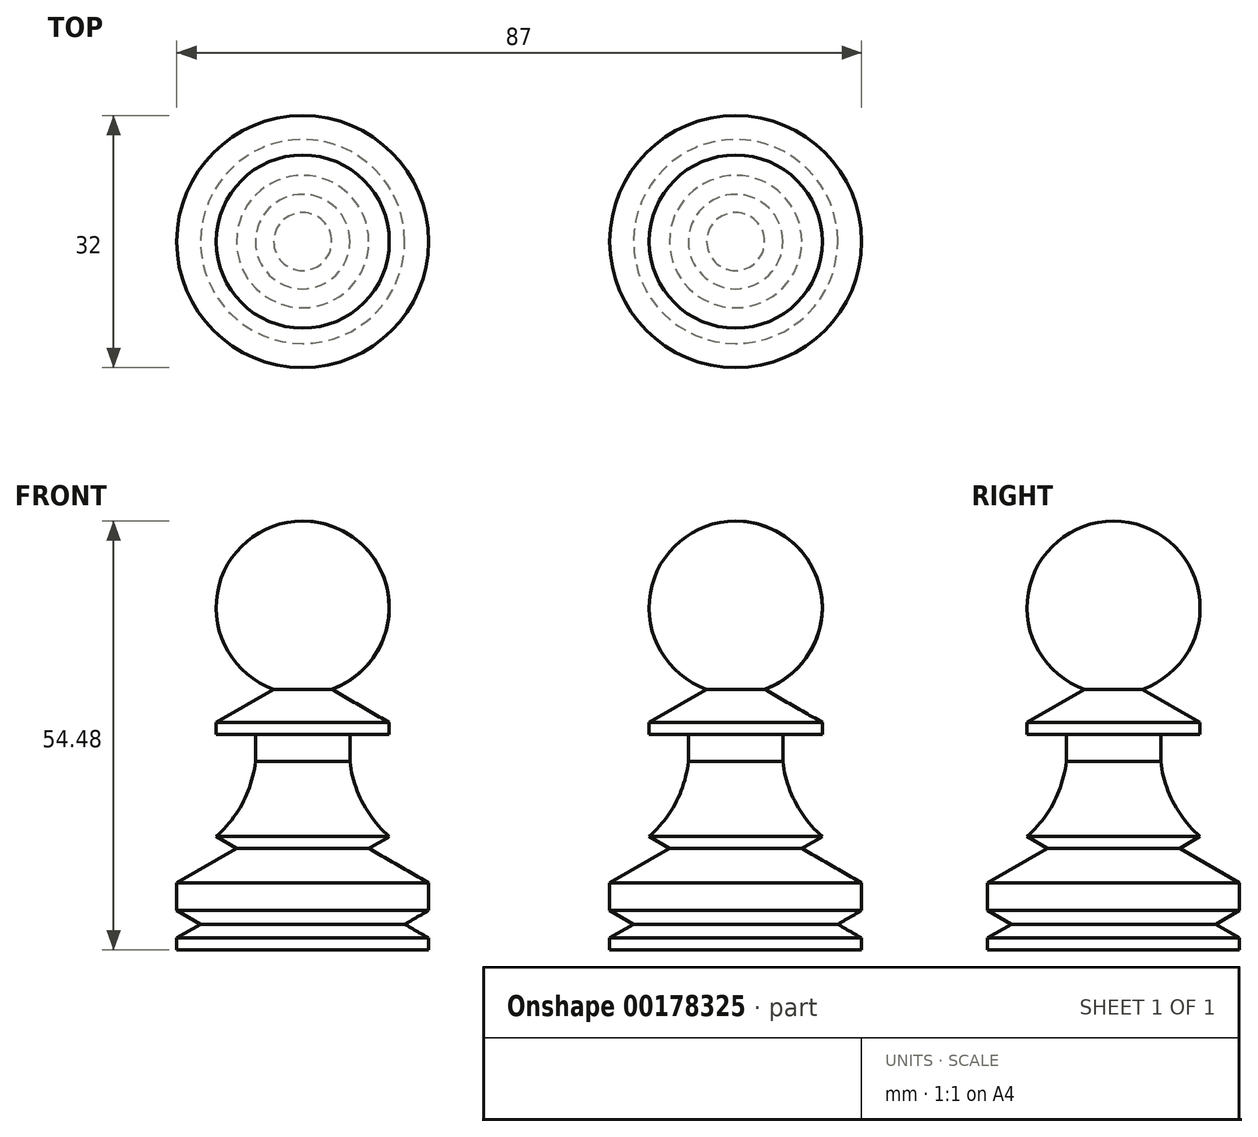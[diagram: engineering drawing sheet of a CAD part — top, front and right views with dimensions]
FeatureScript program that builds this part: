
annotation { "Feature Type Name" : "Feature", "Feature Type Description" : "" }
export const myFeature = defineFeature(function(context is Context, id is Id, definition is map)
    precondition{}
    {
        {
            var Q0;
            Q0=qCreatedBy(makeId("Front.planeOp"),FACE);
            var sketch = newSketch(context, id + "F0", { "sketchPlane" : qUnion([Q0])});
            skLineSegment(sketch, "E0", {"start": v(0, 0) * mm, "end": v(16, 0) * mm});
            skLineSegment(sketch, "E1", {"start": v(16, 0) * mm, "end": v(16, 1.5) * mm});
            skLineSegment(sketch, "E2", {"start": v(16, 1.5) * mm, "end": v(12.97, 3.25) * mm});
            skLineSegment(sketch, "E3", {"start": v(0, 0) * mm, "end": v(0, 5) * mm});
            skLineSegment(sketch, "E4", {"start": v(0, 5) * mm, "end": v(16, 5) * mm});
            skLineSegment(sketch, "E5", {"start": v(16, 5) * mm, "end": v(12.97, 3.25) * mm});
            skPoint(sketch, "E6.orphan", {"position": v(9.94, 1.5) * mm});
            skLineSegment(sketch, "E7", {"start": v(16, 5) * mm, "end": v(16, 8.5) * mm});
            skLineSegment(sketch, "E8", {"start": v(16, 8.5) * mm, "end": v(0, 8.5) * mm});
            skLineSegment(sketch, "E9", {"start": v(16, 8.5) * mm, "end": v(8.4, 12.89) * mm});
            skLineSegment(sketch, "E10", {"start": v(11, 12.89) * mm, "end": v(11, 12.89) * mm});
            skLineSegment(sketch, "E11", {"start": v(11, 56.7) * mm, "end": v(11, 27.39) * mm, "construction": true});
            skLineSegment(sketch, "E12", {"start": v(11, 14.39) * mm, "end": v(0, 14.39) * mm});
            skPoint(sketch, "E13.orphan", {"position": v(16, 13.5) * mm});
            skPoint(sketch, "E14.0.end.orphan", {"position": v(6, 13.5) * mm});
            skLineSegment(sketch, "E15", {"start": v(8.4, 12.89) * mm, "end": v(0, 12.89) * mm});
            skLineSegment(sketch, "E16", {"start": v(0, 14.39) * mm, "end": v(0, 27.39) * mm});
            skLineSegment(sketch, "E17", {"start": v(0, 27.39) * mm, "end": v(11, 27.39) * mm});
            skLineSegment(sketch, "E18", {"start": v(11, 27.39) * mm, "end": v(11, 28.89) * mm});
            skLineSegment(sketch, "E19", {"start": v(11, 28.89) * mm, "end": v(0, 28.89) * mm});
            skLineSegment(sketch, "E20", {"start": v(11, 28.89) * mm, "end": v(3.68, 33.11) * mm});
            skLineSegment(sketch, "E21", {"start": v(6, 27.39) * mm, "end": v(6, 14.39) * mm});
            skArc(sketch, "E22", {"start": v(6, 27.39) * mm, "mid": v(6.9, 20.27) * mm, "end": v(11, 14.39) * mm});
            skPoint(sketch, "E22.third.point", {"position": v(6, 23.93) * mm});
            skArc(sketch, "E23", {"start": v(3.68, 33.11) * mm, "mid": v(10.84, 45.35) * mm, "end": v(0, 54.48) * mm});
            skLineSegment(sketch, "E24", {"start": v(0, 54.48) * mm, "end": v(0, 0) * mm});
            skLineSegment(sketch, "E25", {"start": v(11, 27.39) * mm, "end": v(35.92, 27.39) * mm, "construction": true});
            skLineSegment(sketch, "E26", {"start": v(8.4, 12.89) * mm, "end": v(11, 14.39) * mm});
            skSolve(sketch);
        }
        {
            var Q0;
            Q0 = qSketchRegion(id + "F0", true);
            var Q1;
            Q1=sQuery(id+"F0.wireOp",EDGE,"E24");
            revolve(context, id + "F1", {"entities" : qUnion([Q0]), "axis" : qUnion([Q1]), "revolveType" : RevolveType.FULL});
        }
        {
            var Q0;
            Q0=makeQuery(id+"F1.opRevolve","SWEPT_BODY",BODY,{"disambiguationData":[OSD([sQuery(id+"F0.wireOp",EDGE,"E0"),sQuery(id+"F0.wireOp",EDGE,"E1"),sQuery(id+"F0.wireOp",EDGE,"E2"),sQuery(id+"F0.wireOp",EDGE,"E5"),sQuery(id+"F0.wireOp",EDGE,"E7"),sQuery(id+"F0.wireOp",EDGE,"E9"),sQuery(id+"F0.wireOp",EDGE,"E17"),sQuery(id+"F0.wireOp",EDGE,"E18"),sQuery(id+"F0.wireOp",EDGE,"E20"),sQuery(id+"F0.wireOp",EDGE,"E21"),sQuery(id+"F0.wireOp",EDGE,"E22"),sQuery(id+"F0.wireOp",EDGE,"E23"),sQuery(id+"F0.wireOp",EDGE,"E24"),sQuery(id+"F0.wireOp",EDGE,"E26")])]});
            transform(context, id + "F2", {"entities" : qUnion([Q0]), "transformType" : TransformType.TRANSLATION_3D, "dx" : 0 * mm, "dy" : 0 * mm, "dz" : 0 * mm, "makeCopy" : true});
        }
        {
            var Q0;
            Q0=makeQuery(id+"F2.opPattern","COPY",BODY,{"derivedFrom":makeQuery(id+"F1.opRevolve","SWEPT_BODY",BODY,{"disambiguationData":[OSD([sQuery(id+"F0.wireOp",EDGE,"E0"),sQuery(id+"F0.wireOp",EDGE,"E1"),sQuery(id+"F0.wireOp",EDGE,"E2"),sQuery(id+"F0.wireOp",EDGE,"E5"),sQuery(id+"F0.wireOp",EDGE,"E7"),sQuery(id+"F0.wireOp",EDGE,"E9"),sQuery(id+"F0.wireOp",EDGE,"E17"),sQuery(id+"F0.wireOp",EDGE,"E18"),sQuery(id+"F0.wireOp",EDGE,"E20"),sQuery(id+"F0.wireOp",EDGE,"E21"),sQuery(id+"F0.wireOp",EDGE,"E22"),sQuery(id+"F0.wireOp",EDGE,"E23"),sQuery(id+"F0.wireOp",EDGE,"E24"),sQuery(id+"F0.wireOp",EDGE,"E26")])]}),"instanceName":"1"});
            deleteBodies(context, id + "F3", {"entities" : qUnion([Q0])});
        }
        {
            var Q0;
            Q0=makeQuery(id+"F1.opRevolve","SWEPT_BODY",BODY,{"disambiguationData":[OSD([sQuery(id+"F0.wireOp",EDGE,"E0"),sQuery(id+"F0.wireOp",EDGE,"E1"),sQuery(id+"F0.wireOp",EDGE,"E2"),sQuery(id+"F0.wireOp",EDGE,"E5"),sQuery(id+"F0.wireOp",EDGE,"E7"),sQuery(id+"F0.wireOp",EDGE,"E9"),sQuery(id+"F0.wireOp",EDGE,"E17"),sQuery(id+"F0.wireOp",EDGE,"E18"),sQuery(id+"F0.wireOp",EDGE,"E20"),sQuery(id+"F0.wireOp",EDGE,"E21"),sQuery(id+"F0.wireOp",EDGE,"E22"),sQuery(id+"F0.wireOp",EDGE,"E23"),sQuery(id+"F0.wireOp",EDGE,"E24"),sQuery(id+"F0.wireOp",EDGE,"E26")])]});
            transform(context, id + "F4", {"entities" : qUnion([Q0]), "transformType" : TransformType.TRANSLATION_3D, "dx" : 55 * mm, "dy" : 0 * mm, "dz" : 0 * mm, "makeCopy" : true});
        }
    });
